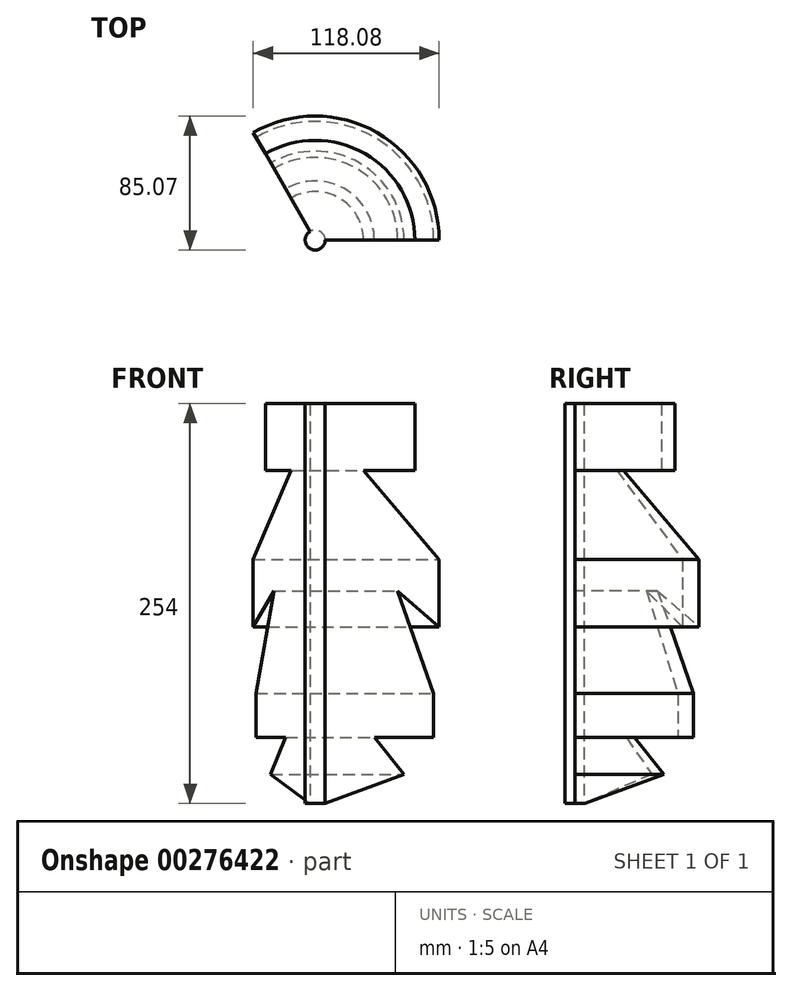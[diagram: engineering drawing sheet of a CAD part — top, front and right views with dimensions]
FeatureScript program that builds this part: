
annotation { "Feature Type Name" : "Feature", "Feature Type Description" : "" }
export const myFeature = defineFeature(function(context is Context, id is Id, definition is map)
    precondition{}
    {
        {
            var Q0;
            Q0=qCreatedBy(makeId("Top.planeOp"),FACE);
            var sketch = newSketch(context, id + "F0", { "sketchPlane" : qUnion([Q0])});
            skCircle(sketch, "E0", {"center": v(0, 0) * mm, "radius": 6.35 * mm});
            skSolve(sketch);
        }
        {
            var Q0;
            Q0 = qSketchRegion(id + "F0", true);
            extrude(context, id + "F1", {"entities" : qUnion([Q0]), "depth" : 254 * mm});
        }
        {
            var Q0;
            Q0=qCreatedBy(makeId("Front.planeOp"),FACE);
            var sketch = newSketch(context, id + "F2", { "sketchPlane" : qUnion([Q0])});
            skLineSegment(sketch, "E1", {"start": v(6.35, 254) * mm, "end": v(6.35, 0) * mm});
            skLineSegment(sketch, "E2", {"start": v(6.35, 254) * mm, "end": v(63.3, 254) * mm});
            skLineSegment(sketch, "E3", {"start": v(63.3, 254) * mm, "end": v(63.3, 211.57) * mm});
            skLineSegment(sketch, "E4", {"start": v(63.3, 211.57) * mm, "end": v(30.71, 211.57) * mm});
            skLineSegment(sketch, "E5", {"start": v(30.71, 211.57) * mm, "end": v(78.72, 154.98) * mm});
            skLineSegment(sketch, "E6", {"start": v(78.72, 154.98) * mm, "end": v(78.72, 112.12) * mm});
            skLineSegment(sketch, "E7", {"start": v(78.72, 112.12) * mm, "end": v(52.43, 134.98) * mm});
            skLineSegment(sketch, "E8", {"start": v(52.43, 134.98) * mm, "end": v(75.3, 69.82) * mm});
            skLineSegment(sketch, "E9", {"start": v(75.3, 69.82) * mm, "end": v(75.3, 41.82) * mm});
            skLineSegment(sketch, "E10", {"start": v(75.3, 41.82) * mm, "end": v(37.57, 41.82) * mm});
            skLineSegment(sketch, "E11", {"start": v(37.57, 41.82) * mm, "end": v(56.43, 18.38) * mm});
            skLineSegment(sketch, "E12", {"start": v(56.43, 18.38) * mm, "end": v(6.35, 0) * mm});
            skLineSegment(sketch, "E13", {"start": v(0, 297.3) * mm, "end": v(0, -54.78) * mm, "construction": true});
            skSolve(sketch);
        }
        {
            var Q0;
            Q0=makeQuery(id+"F2.imprint","IMPRINT",FACE,{"disambiguationData":[TD([[makeQuery(id+"F2.imprint","IMPRINT",EDGE,{"derivedFrom":sQuery(id+"F2.wireOp",EDGE,"E1")}),1.0]])]});
            var Q1;
            Q1=sQuery(id+"F2.wireOp",EDGE,"E13");
            revolve(context, id + "F3", {"operationType" : NewBodyOperationType.ADD, "entities" : qUnion([Q0]), "axis" : qUnion([Q1]), "revolveType" : RevolveType.ONE_DIRECTION, "oppositeDirection" : true, "angle" : 120 * degree});
        }
    });
